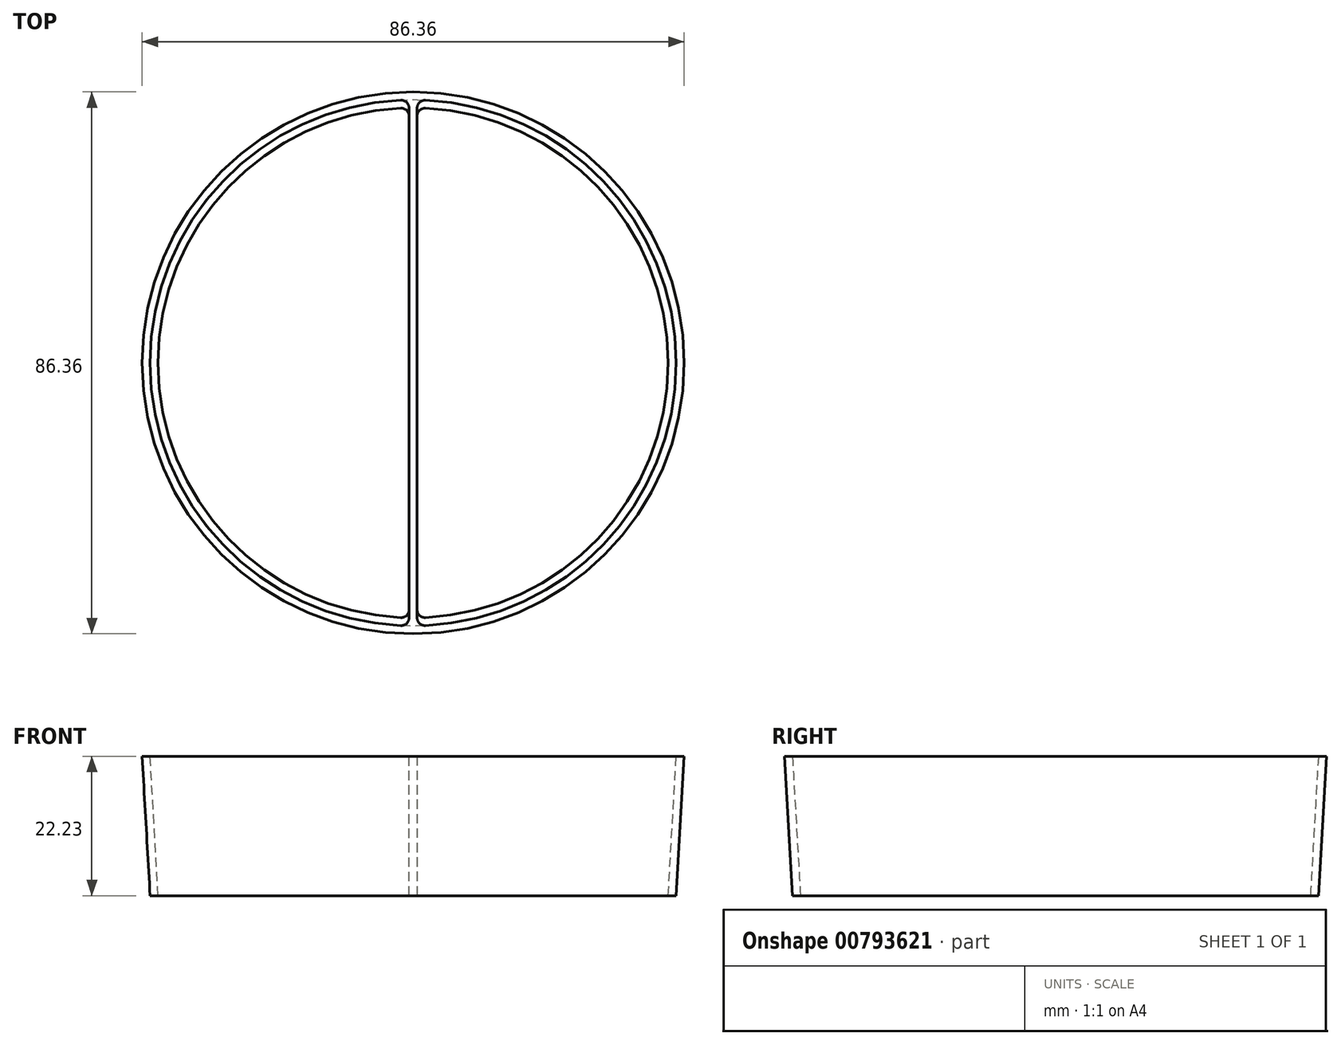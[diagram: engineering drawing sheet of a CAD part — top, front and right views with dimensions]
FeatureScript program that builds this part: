
annotation { "Feature Type Name" : "Feature", "Feature Type Description" : "" }
export const myFeature = defineFeature(function(context is Context, id is Id, definition is map)
    precondition{}
    {
        {
            var Q0;
            Q0=qCreatedBy(makeId("Front.planeOp"),FACE);
            var sketch = newSketch(context, id + "F0", { "sketchPlane" : qUnion([Q0])});
            skLineSegment(sketch, "E0", {"start": v(0, 0) * mm, "end": v(41.91, 0) * mm});
            skLineSegment(sketch, "E1", {"start": v(41.9, 0) * mm, "end": v(43.18, 22.23) * mm});
            skLineSegment(sketch, "E2", {"start": v(43.18, 22.23) * mm, "end": v(41.9, 22.23) * mm});
            skLineSegment(sketch, "E3", {"start": v(41.9, 22.23) * mm, "end": v(40.64, 0) * mm});
            skLineSegment(sketch, "E4", {"start": v(0, 0) * mm, "end": v(0, 8.22) * mm});
            skSolve(sketch);
        }
        {
            var Q0;
            {var subQ0=sQuery(id+"F0.wireOp",EDGE,"E1");Q0=makeQuery(id+"F0.imprint","IMPRINT",FACE,{"disambiguationData":[TD([[makeQuery(id+"F0.imprint","IMPRINT",EDGE,{"derivedFrom":subQ0}),1.0]])]});}
            var Q1;
            Q1=sQuery(id+"F0.wireOp",EDGE,"E4");
            revolve(context, id + "F1", {"surfaceOperationType" : NewSurfaceOperationType.NEW, "entities" : qUnion([Q0]), "axis" : qUnion([Q1]), "revolveType" : RevolveType.FULL});
        }
        {
            var Q0;
            Q0=qCreatedBy(makeId("Top.planeOp"),FACE);
            var sketch = newSketch(context, id + "F2", { "sketchPlane" : qUnion([Q0])});
            skLineSegment(sketch, "E5.bottom", {"start": v(-0.64, 50.8) * mm, "end": v(0.63, 50.8) * mm});
            skLineSegment(sketch, "E5.left", {"start": v(-0.64, 41.9) * mm, "end": v(-0.63, -41.9) * mm});
            skLineSegment(sketch, "E5.right", {"start": v(0.63, 41.9) * mm, "end": v(0.64, -41.9) * mm});
            skCircle(sketch, "E6.0", {"center": v(0, 0) * mm, "radius": 43.18 * mm});
            skCircle(sketch, "E7.0", {"center": v(0, 0) * mm, "radius": 41.91 * mm});
            skSolve(sketch);
        }
        {
            var Q0;
            {var subQ0=sQuery(id+"F2.wireOp",EDGE,"E5.left");Q0=makeQuery(id+"F2.imprint","IMPRINT",FACE,{"disambiguationData":[TD([[makeQuery(id+"F2.imprint","IMPRINT",EDGE,{"derivedFrom":subQ0}),1.0]])]});}
            var Q1;
            Q1=makeQuery(id+"F1.opRevolve","SWEPT_FACE",FACE,{"disambiguationData":[OSD([sQuery(id+"F0.wireOp",EDGE,"E2")])]});
            extrude(context, id + "F3", {"entities" : qUnion([Q0]), "operationType" : NewBodyOperationType.ADD, "endBound" : BoundingType.UP_TO_SURFACE, "depth" : 25.4 * mm, "endBoundEntityFace" : qUnion([Q1]), "offsetDistance" : 25.4 * mm});
        }
        {
            var Q0;
            Q0=makeQuery(id+"F3.boolean.opBoolean","INTERSECT",EDGE,{"disambiguationData":[OD(1.0)],"derivedFrom":[makeQuery(id+"F1.opRevolve","SWEPT_FACE",FACE,{"disambiguationData":[OSD([sQuery(id+"F0.wireOp",EDGE,"E3")])]}),makeQuery(id+"F3.opExtrude","SWEPT_FACE",FACE,{"disambiguationData":[OSD([sQuery(id+"F2.wireOp",EDGE,"E5.right")])]})]});
            var Q1;
            Q1=makeQuery(id+"F3.boolean.opBoolean","INTERSECT",EDGE,{"disambiguationData":[OD(1.0)],"derivedFrom":[makeQuery(id+"F1.opRevolve","SWEPT_FACE",FACE,{"disambiguationData":[OSD([sQuery(id+"F0.wireOp",EDGE,"E3")])]}),makeQuery(id+"F3.opExtrude","SWEPT_FACE",FACE,{"disambiguationData":[OSD([sQuery(id+"F2.wireOp",EDGE,"E5.left")])]})]});
            var Q2;
            Q2=makeQuery(id+"F3.boolean.opBoolean","INTERSECT",EDGE,{"disambiguationData":[OD(0.0)],"derivedFrom":[makeQuery(id+"F1.opRevolve","SWEPT_FACE",FACE,{"disambiguationData":[OSD([sQuery(id+"F0.wireOp",EDGE,"E3")])]}),makeQuery(id+"F3.opExtrude","SWEPT_FACE",FACE,{"disambiguationData":[OSD([sQuery(id+"F2.wireOp",EDGE,"E5.right")])]})]});
            var Q3;
            Q3=makeQuery(id+"F3.boolean.opBoolean","INTERSECT",EDGE,{"disambiguationData":[OD(0.0)],"derivedFrom":[makeQuery(id+"F1.opRevolve","SWEPT_FACE",FACE,{"disambiguationData":[OSD([sQuery(id+"F0.wireOp",EDGE,"E3")])]}),makeQuery(id+"F3.opExtrude","SWEPT_FACE",FACE,{"disambiguationData":[OSD([sQuery(id+"F2.wireOp",EDGE,"E5.left")])]})]});
            fillet(context, id + "F4", {"entities" : qUnion([Q0, Q1, Q2, Q3]), "radius" : 1.27 * mm, "tangentPropagation" : true, "allowEdgeOverflow" : false});
        }
    });
